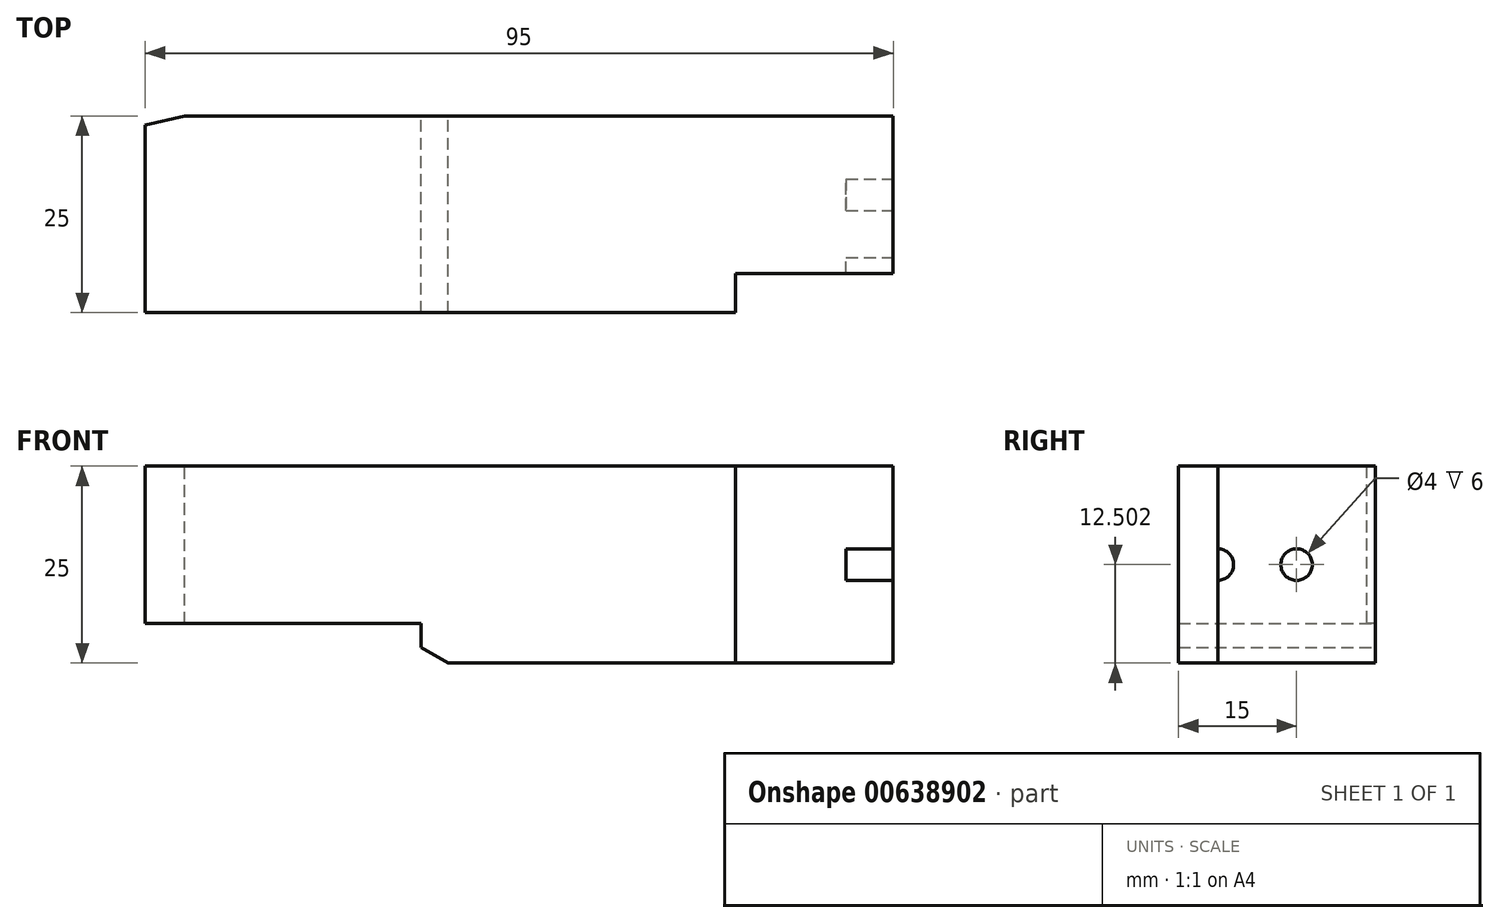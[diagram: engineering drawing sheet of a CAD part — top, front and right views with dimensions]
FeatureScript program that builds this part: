
annotation { "Feature Type Name" : "Feature", "Feature Type Description" : "" }
export const myFeature = defineFeature(function(context is Context, id is Id, definition is map)
    precondition{}
    {
        {
            var Q0;
            Q0=qCreatedBy(makeId("Front.planeOp"),FACE);
            var sketch = newSketch(context, id + "F0", { "sketchPlane" : qUnion([Q0])});
            skLineSegment(sketch, "E0", {"start": v(71.39, -70.2) * mm, "end": v(71.39, -95.2) * mm});
            skLineSegment(sketch, "E1", {"start": v(-20.15, -90.2) * mm, "end": v(-20.15, -70.2) * mm});
            skLineSegment(sketch, "E2", {"start": v(-23.61, -70.2) * mm, "end": v(-23.61, -90.2) * mm});
            skLineSegment(sketch, "E3", {"start": v(71.39, -95.2) * mm, "end": v(14.85, -95.2) * mm});
            skLineSegment(sketch, "E4", {"start": v(11.39, -90.2) * mm, "end": v(11.39, -93.2) * mm});
            skLineSegment(sketch, "E5", {"start": v(11.39, -93.2) * mm, "end": v(14.85, -95.2) * mm});
            skLineSegment(sketch, "E6", {"start": v(11.39, -90.2) * mm, "end": v(-23.61, -90.2) * mm});
            skLineSegment(sketch, "E7", {"start": v(71.39, -70.2) * mm, "end": v(-23.61, -70.2) * mm});
            skLineSegment(sketch, "E8", {"start": v(63.52, -82.7) * mm, "end": v(72.1, -82.7) * mm});
            skLineSegment(sketch, "E9", {"start": v(65.39, -80.7) * mm, "end": v(64.23, -82.7) * mm});
            skLineSegment(sketch, "E10", {"start": v(65.39, -84.7) * mm, "end": v(64.23, -82.7) * mm});
            skLineSegment(sketch, "E11", {"start": v(65.39, -84.7) * mm, "end": v(71.39, -84.7) * mm});
            skLineSegment(sketch, "E12", {"start": v(65.39, -80.7) * mm, "end": v(65.39, -84.7) * mm});
            skLineSegment(sketch, "E13", {"start": v(71.39, -80.7) * mm, "end": v(65.39, -80.7) * mm});
            skLineSegment(sketch, "E14", {"start": v(49.39, -75.2) * mm, "end": v(73.39, -75.2) * mm});
            skLineSegment(sketch, "E15", {"start": v(49.39, -90.2) * mm, "end": v(73.39, -90.2) * mm});
            skLineSegment(sketch, "E16", {"start": v(51.39, -70.2) * mm, "end": v(51.39, -95.2) * mm});
            skLineSegment(sketch, "E17", {"start": v(-48.39, -95.2) * mm, "end": v(-48.39, -70.2) * mm});
            skLineSegment(sketch, "E18", {"start": v(-73.39, -95.2) * mm, "end": v(-48.39, -95.2) * mm});
            skLineSegment(sketch, "E19", {"start": v(-73.39, -70.2) * mm, "end": v(-48.39, -70.2) * mm});
            skCircle(sketch, "E20", {"center": v(-53.39, -90.2) * mm, "radius": 2.5 * mm});
            skCircle(sketch, "E21", {"center": v(-53.39, -75.2) * mm, "radius": 2.5 * mm});
            skCircle(sketch, "E22", {"center": v(-53.39, -82.7) * mm, "radius": 2 * mm});
            skCircle(sketch, "E23", {"center": v(-63.39, -82.7) * mm, "radius": 2 * mm});
            skLineSegment(sketch, "E24", {"start": v(-73.39, -90.2) * mm, "end": v(-58.39, -90.2) * mm});
            skLineSegment(sketch, "E25", {"start": v(-73.39, -93.2) * mm, "end": v(-58.39, -93.2) * mm});
            skLineSegment(sketch, "E26", {"start": v(-71.39, -90.2) * mm, "end": v(-71.39, -70.2) * mm});
            skLineSegment(sketch, "E27", {"start": v(-73.39, -95.2) * mm, "end": v(-73.39, -70.2) * mm});
            skLineSegment(sketch, "E28", {"start": v(-58.39, -95.2) * mm, "end": v(-58.39, -70.2) * mm});
            skLineSegment(sketch, "E29", {"start": v(-58.39, -1.8) * mm, "end": v(-71.39, -1.8) * mm});
            skLineSegment(sketch, "E30", {"start": v(-48.39, 93.2) * mm, "end": v(-73.39, 93.2) * mm});
            skLineSegment(sketch, "E31", {"start": v(-48.39, 93.2) * mm, "end": v(-48.39, 73.2) * mm});
            skLineSegment(sketch, "E32", {"start": v(-73.39, 93.2) * mm, "end": v(-73.39, 1.66) * mm});
            skLineSegment(sketch, "E33", {"start": v(-48.39, 73.2) * mm, "end": v(-58.39, 73.2) * mm});
            skLineSegment(sketch, "E34", {"start": v(-58.39, -1.8) * mm, "end": v(-58.39, 73.2) * mm});
            skLineSegment(sketch, "E35", {"start": v(-53.39, 71.2) * mm, "end": v(-53.39, 95.2) * mm});
            skLineSegment(sketch, "E36", {"start": v(-53.39, 85.33) * mm, "end": v(-53.39, 93.91) * mm});
            skLineSegment(sketch, "E37", {"start": v(-58.39, 33.2) * mm, "end": v(-73.39, 33.2) * mm});
            skLineSegment(sketch, "E38", {"start": v(-71.39, -1.8) * mm, "end": v(-73.39, 1.66) * mm});
            skSolve(sketch);
        }
        {
            var Q0;
            {var subQ0=sQuery(id+"F0.wireOp",EDGE,"E13");Q0=makeQuery(id+"F0.imprint","IMPRINT",FACE,{"disambiguationData":[TD([[makeQuery(id+"F0.imprint","IMPRINT",EDGE,{"derivedFrom":subQ0}),1.0]])]});}
            var Q1;
            {var subQ0=sQuery(id+"F0.wireOp",EDGE,"E11");Q1=makeQuery(id+"F0.imprint","IMPRINT",FACE,{"disambiguationData":[TD([[makeQuery(id+"F0.imprint","IMPRINT",EDGE,{"derivedFrom":subQ0}),1.0]])]});}
            var Q2;
            {var subQ5=sQuery(id+"F0.wireOp",EDGE,"E1");Q2=makeQuery(id+"F0.imprint","IMPRINT",FACE,{"disambiguationData":[TD([[makeQuery(id+"F0.imprint","IMPRINT",EDGE,{"derivedFrom":subQ5}),-1.0]])]});}
            var Q3;
            {var subQ0=sQuery(id+"F0.wireOp",EDGE,"E1");Q3=makeQuery(id+"F0.imprint","IMPRINT",FACE,{"disambiguationData":[TD([[makeQuery(id+"F0.imprint","IMPRINT",EDGE,{"derivedFrom":subQ0}),1.0]])]});}
            var Q4;
            {var subQ0=sQuery(id+"F0.wireOp",EDGE,"E7");var subQ1=sQuery(id+"F0.wireOp",EDGE,"E0");var subQ2=makeQuery(id+"F0.imprint","INTERSECT",VERTEX,{"derivedFrom":[subQ1,subQ0]});Q4=makeQuery(id+"F0.imprint","IMPRINT",FACE,{"disambiguationData":[TD([[makeQuery(id+"F0.imprint","IMPRINT",EDGE,{"disambiguationData":[TD([[subQ2,-1.0]])],"derivedFrom":subQ1}),-1.0]])]});}
            var Q5;
            {var subQ0=sQuery(id+"F0.wireOp",EDGE,"E3");var subQ1=sQuery(id+"F0.wireOp",EDGE,"E0");var subQ2=makeQuery(id+"F0.imprint","INTERSECT",VERTEX,{"derivedFrom":[subQ1,subQ0]});Q5=makeQuery(id+"F0.imprint","IMPRINT",FACE,{"disambiguationData":[TD([[makeQuery(id+"F0.imprint","IMPRINT",EDGE,{"disambiguationData":[TD([[subQ2,1.0]])],"derivedFrom":subQ1}),-1.0]])]});}
            var Q6;
            Q6=makeQuery(id+"F0.imprint","IMPRINT",FACE,{"disambiguationData":[TD([[makeQuery(id+"F0.imprint","IMPRINT",EDGE,{"derivedFrom":sQuery(id+"F0.wireOp",EDGE,"E9")}),-1.0]])]});
            var Q7;
            {var subQ0=sQuery(id+"F0.wireOp",EDGE,"E9");Q7=makeQuery(id+"F0.imprint","IMPRINT",FACE,{"disambiguationData":[TD([[makeQuery(id+"F0.imprint","IMPRINT",EDGE,{"derivedFrom":subQ0}),1.0]])]});}
            var Q8;
            {var subQ0=sQuery(id+"F0.wireOp",EDGE,"E10");Q8=makeQuery(id+"F0.imprint","IMPRINT",FACE,{"disambiguationData":[TD([[makeQuery(id+"F0.imprint","IMPRINT",EDGE,{"derivedFrom":subQ0}),-1.0]])]});}
            extrude(context, id + "F1", {"entities" : qUnion([Q0, Q1, Q2, Q3, Q4, Q5, Q6, Q7, Q8]), "depth" : 25 * mm, "offsetDistance" : 25 * mm});
        }
        {
            var Q0;
            Q0=makeQuery(id+"F1.opExtrude","SWEPT_FACE",FACE,{"disambiguationData":[OSD([sQuery(id+"F0.wireOp",EDGE,"E7")])]});
            var sketch = newSketch(context, id + "F2", { "sketchPlane" : qUnion([Q0])});
            skPoint(sketch, "E39.0", {"position": v(16.66, -19.73) * mm});
            skLineSegment(sketch, "E40.0", {"start": v(71.39, -25) * mm, "end": v(71.39, 0) * mm});
            skLineSegment(sketch, "E41.0", {"start": v(71.39, 0) * mm, "end": v(-23.61, 0) * mm});
            skLineSegment(sketch, "E42.0", {"start": v(-23.61, -25) * mm, "end": v(-23.61, 0) * mm});
            skLineSegment(sketch, "E43.0", {"start": v(71.39, -25) * mm, "end": v(-23.61, -25) * mm});
            skLineSegment(sketch, "E44", {"start": v(-23.61, -15) * mm, "end": v(-23.61, -2) * mm});
            skLineSegment(sketch, "E45", {"start": v(71.39, -25) * mm, "end": v(51.39, -25) * mm});
            skLineSegment(sketch, "E46", {"start": v(71.39, 0) * mm, "end": v(-20.15, 0) * mm});
            skLineSegment(sketch, "E47", {"start": v(51.39, -25) * mm, "end": v(51.39, -15) * mm});
            skLineSegment(sketch, "E48", {"start": v(-23.61, -15) * mm, "end": v(51.39, -15) * mm});
            skLineSegment(sketch, "E49", {"start": v(49.39, -20) * mm, "end": v(73.39, -20) * mm});
            skLineSegment(sketch, "E50", {"start": v(63.52, -20) * mm, "end": v(72.1, -20) * mm});
            skLineSegment(sketch, "E51", {"start": v(11.39, -15) * mm, "end": v(11.39, 0) * mm});
            skLineSegment(sketch, "E52", {"start": v(-23.61, -2) * mm, "end": v(-20.15, 0) * mm});
            skLineSegment(sketch, "E53", {"start": v(-105.14, -204.45) * mm, "end": v(-118.14, -204.45) * mm});
            skLineSegment(sketch, "E54", {"start": v(-95.14, -109.45) * mm, "end": v(-120.14, -109.45) * mm});
            skLineSegment(sketch, "E55", {"start": v(-95.14, -109.45) * mm, "end": v(-95.14, -129.45) * mm});
            skLineSegment(sketch, "E56", {"start": v(-120.14, -109.45) * mm, "end": v(-120.14, -200.98) * mm});
            skLineSegment(sketch, "E57", {"start": v(-95.14, -129.45) * mm, "end": v(-105.14, -129.45) * mm});
            skLineSegment(sketch, "E58", {"start": v(-105.14, -204.45) * mm, "end": v(-105.14, -129.45) * mm});
            skLineSegment(sketch, "E59", {"start": v(-100.14, -131.45) * mm, "end": v(-100.14, -107.45) * mm});
            skLineSegment(sketch, "E60", {"start": v(-100.14, -117.32) * mm, "end": v(-100.14, -108.73) * mm});
            skLineSegment(sketch, "E61", {"start": v(-105.14, -169.45) * mm, "end": v(-120.14, -169.45) * mm});
            skLineSegment(sketch, "E62", {"start": v(-118.14, -204.45) * mm, "end": v(-120.14, -200.98) * mm});
            skSolve(sketch);
        }
        {
            var Q0;
            {var subQ1=sQuery(id+"F2.wireOp",EDGE,"E43.0");Q0=makeQuery(id+"F2.imprint","IMPRINT",FACE,{"disambiguationData":[TD([[makeQuery(id+"F2.imprint","IMPRINT",EDGE,{"derivedFrom":subQ1}),-1.0]])]});}
            extrude(context, id + "F3", {"entities" : qUnion([Q0]), "operationType" : NewBodyOperationType.REMOVE, "endBound" : BoundingType.THROUGH_ALL, "oppositeDirection" : true, "depth" : 25 * mm, "offsetDistance" : 25 * mm});
        }
        {
            var Q0;
            Q0=makeQuery(id+"F3.boolean.opBoolean","COPY",FACE,{"derivedFrom":makeQuery(id+"F3.opExtrude","SWEPT_FACE",FACE,{"disambiguationData":[OSD([sQuery(id+"F2.wireOp",EDGE,"E47")])]})});
            var sketch = newSketch(context, id + "F4", { "sketchPlane" : qUnion([Q0])});
            skLineSegment(sketch, "E63.0", {"start": v(25, -70.2) * mm, "end": v(15, -70.2) * mm});
            skLineSegment(sketch, "E64.0", {"start": v(25, -95.2) * mm, "end": v(25, -70.2) * mm});
            skLineSegment(sketch, "E65.0.0", {"start": v(15, -95.2) * mm, "end": v(25, -95.2) * mm});
            skLineSegment(sketch, "E65.0.3", {"start": v(15, -70.2) * mm, "end": v(15, -95.2) * mm});
            skLineSegment(sketch, "E66", {"start": v(0, -95.2) * mm, "end": v(25, -95.2) * mm});
            skLineSegment(sketch, "E67", {"start": v(0, -70.2) * mm, "end": v(25, -70.2) * mm});
            skCircle(sketch, "E68", {"center": v(20, -90.2) * mm, "radius": 2.5 * mm});
            skCircle(sketch, "E69", {"center": v(20, -75.2) * mm, "radius": 2.5 * mm});
            skCircle(sketch, "E70", {"center": v(20, -82.7) * mm, "radius": 2 * mm});
            skCircle(sketch, "E71", {"center": v(10, -82.7) * mm, "radius": 2 * mm});
            skLineSegment(sketch, "E72", {"start": v(0, -90.2) * mm, "end": v(15, -90.2) * mm});
            skLineSegment(sketch, "E73", {"start": v(0, -93.2) * mm, "end": v(15, -93.2) * mm});
            skLineSegment(sketch, "E74", {"start": v(2, -90.2) * mm, "end": v(2, -70.2) * mm});
            skLineSegment(sketch, "E75", {"start": v(0, -95.2) * mm, "end": v(0, -70.2) * mm});
            skLineSegment(sketch, "E76", {"start": v(15, -95.2) * mm, "end": v(15, -70.2) * mm});
            skSolve(sketch);
        }
        {
            var Q0;
            Q0=makeQuery(id+"F4.imprint","IMPRINT",FACE,{"disambiguationData":[TD([[makeQuery(id+"F4.imprint","IMPRINT",EDGE,{"derivedFrom":sQuery(id+"F4.wireOp",EDGE,"E69")}),-1.0]])]});
            var Q1;
            Q1=makeQuery(id+"F4.imprint","IMPRINT",FACE,{"disambiguationData":[TD([[makeQuery(id+"F4.imprint","IMPRINT",EDGE,{"derivedFrom":sQuery(id+"F4.wireOp",EDGE,"E68")}),-1.0]])]});
            extrude(context, id + "F5", {"entities" : qUnion([Q0, Q1]), "operationType" : NewBodyOperationType.REMOVE, "endBound" : BoundingType.THROUGH_ALL, "oppositeDirection" : true, "depth" : 25 * mm, "offsetDistance" : 25 * mm});
        }
        {
            var Q0;
            Q0=makeQuery(id+"F1.opExtrude","SWEPT_FACE",FACE,{"disambiguationData":[OSD([sQuery(id+"F0.wireOp",EDGE,"E0")])]});
            var sketch = newSketch(context, id + "F6", { "sketchPlane" : qUnion([Q0])});
            skCircle(sketch, "E77.0", {"center": v(-20, -82.7) * mm, "radius": 2 * mm});
            skCircle(sketch, "E78.0", {"center": v(-10, -82.7) * mm, "radius": 2 * mm});
            skSolve(sketch);
        }
        {
            var Q0;
            Q0=makeQuery(id+"F6.imprint","IMPRINT",FACE,{"disambiguationData":[TD([[makeQuery(id+"F6.imprint","IMPRINT",EDGE,{"derivedFrom":sQuery(id+"F6.wireOp",EDGE,"E77.0")}),1.0]])]});
            var Q1;
            Q1=makeQuery(id+"F6.imprint","IMPRINT",FACE,{"disambiguationData":[TD([[makeQuery(id+"F6.imprint","IMPRINT",EDGE,{"derivedFrom":sQuery(id+"F6.wireOp",EDGE,"E78.0")}),1.0]])]});
            extrude(context, id + "F7", {"entities" : qUnion([Q0, Q1]), "operationType" : NewBodyOperationType.REMOVE, "oppositeDirection" : true, "depth" : 6 * mm, "offsetDistance" : 25 * mm});
        }
        {
            var Q0;
            Q0=makeQuery(id+"F1.opExtrude","CAP_EDGE",EDGE,{"disambiguationData":[OSD([sQuery(id+"F0.wireOp",EDGE,"E2")])],"isStart":true});
            chamfer(context, id + "F8", {"entities" : qUnion([Q0]), "chamferType" : ChamferType.OFFSET_ANGLE, "width" : 5 * mm, "oppositeDirection" : true, "angle" : 13 * degree, "tangentPropagation" : true});
        }
    });
